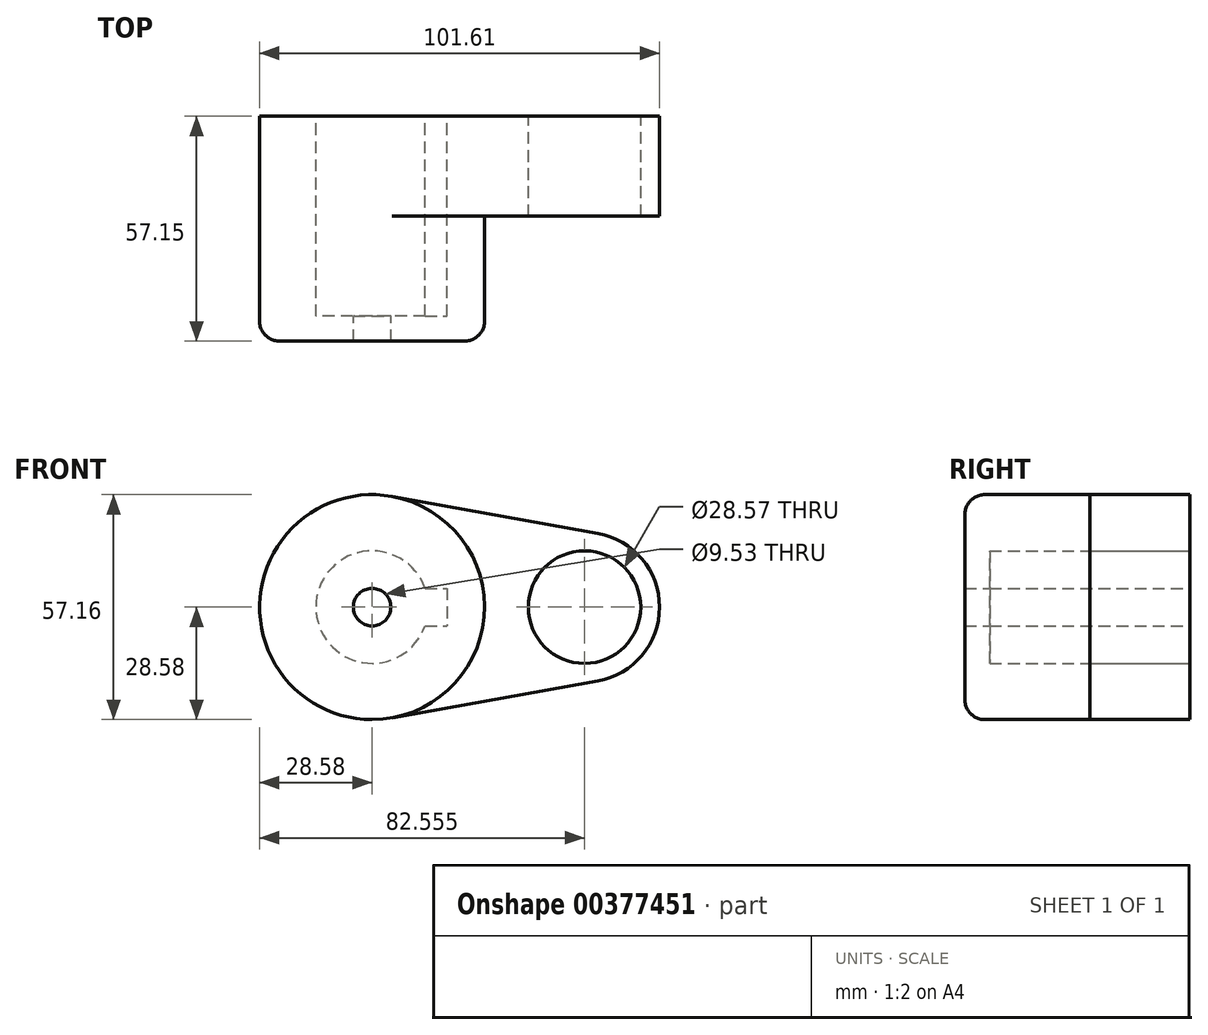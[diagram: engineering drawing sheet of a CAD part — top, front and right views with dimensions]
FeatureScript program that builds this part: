
annotation { "Feature Type Name" : "Feature", "Feature Type Description" : "" }
export const myFeature = defineFeature(function(context is Context, id is Id, definition is map)
    precondition{}
    {
        {
            var Q0;
            Q0=qCreatedBy(makeId("Front.planeOp"),FACE);
            var sketch = newSketch(context, id + "F0", { "sketchPlane" : qUnion([Q0])});
            skCircle(sketch, "E0", {"center": v(0, 0) * mm, "radius": 28.58 * mm});
            skCircle(sketch, "E1", {"center": v(53.97, 0) * mm, "radius": 19.05 * mm});
            skLineSegment(sketch, "E2", {"start": v(5.04, 28.13) * mm, "end": v(57.34, 18.75) * mm});
            skLineSegment(sketch, "E3", {"start": v(5.04, -28.13) * mm, "end": v(57.34, -18.75) * mm});
            skCircle(sketch, "E4", {"center": v(0, 0) * mm, "radius": 14.29 * mm});
            skCircle(sketch, "E5", {"center": v(53.97, 0) * mm, "radius": 14.29 * mm});
            skLineSegment(sketch, "E6.bottom", {"start": v(-19.05, 4.76) * mm, "end": v(19.05, 4.76) * mm});
            skLineSegment(sketch, "E6.top", {"start": v(-19.05, -4.76) * mm, "end": v(19.05, -4.76) * mm});
            skLineSegment(sketch, "E6.left", {"start": v(-19.05, 4.76) * mm, "end": v(-19.05, -4.76) * mm});
            skLineSegment(sketch, "E6.right", {"start": v(19.05, 4.76) * mm, "end": v(19.05, -4.76) * mm});
            skSolve(sketch);
        }
        {
            var Q0;
            {var subQ7=sQuery(id+"F0.wireOp",EDGE,"E6.left");Q0=makeQuery(id+"F0.imprint","IMPRINT",FACE,{"disambiguationData":[TD([[makeQuery(id+"F0.imprint","IMPRINT",EDGE,{"derivedFrom":subQ7}),-1.0]])]});}
            var Q1;
            {var subQ0=sQuery(id+"F0.wireOp",EDGE,"E2");Q1=makeQuery(id+"F0.imprint","IMPRINT",FACE,{"disambiguationData":[TD([[makeQuery(id+"F0.imprint","IMPRINT",EDGE,{"derivedFrom":subQ0}),-1.0]])]});}
            var Q2;
            Q2=makeQuery(id+"F0.imprint","IMPRINT",FACE,{"disambiguationData":[TD([[makeQuery(id+"F0.imprint","IMPRINT",EDGE,{"derivedFrom":sQuery(id+"F0.wireOp",EDGE,"E5")}),-1.0]])]});
            extrude(context, id + "F1", {"entities" : qUnion([Q0, Q1, Q2]), "depth" : 25.4 * mm});
        }
        {
            var Q0;
            {var subQ5=sQuery(id+"F0.wireOp",EDGE,"E6.left");Q0=makeQuery(id+"F0.imprint","IMPRINT",FACE,{"disambiguationData":[TD([[makeQuery(id+"F0.imprint","IMPRINT",EDGE,{"derivedFrom":subQ5}),1.0]])]});}
            var Q1;
            {var subQ7=sQuery(id+"F0.wireOp",EDGE,"E6.left");Q1=makeQuery(id+"F0.imprint","IMPRINT",FACE,{"disambiguationData":[TD([[makeQuery(id+"F0.imprint","IMPRINT",EDGE,{"derivedFrom":subQ7}),-1.0]])]});}
            extrude(context, id + "F2", {"entities" : qUnion([Q0, Q1]), "operationType" : NewBodyOperationType.ADD, "depth" : 50.8 * mm});
        }
        {
            var Q0;
            Q0=makeQuery(id+"F2.opExtrude","CAP_FACE",FACE,{"disambiguationData":[OSD([sQuery(id+"F0.wireOp",EDGE,"E0"),sQuery(id+"F0.wireOp",EDGE,"E4"),sQuery(id+"F0.wireOp",EDGE,"E6.bottom"),sQuery(id+"F0.wireOp",EDGE,"E6.top"),sQuery(id+"F0.wireOp",EDGE,"E6.right")])],"isStart":false});
            var sketch = newSketch(context, id + "F3", { "sketchPlane" : qUnion([Q0])});
            skCircle(sketch, "E7", {"center": v(0, 0) * mm, "radius": 28.58 * mm});
            skCircle(sketch, "E8", {"center": v(0, 0) * mm, "radius": 4.76 * mm});
            skSolve(sketch);
        }
        {
            var Q0;
            Q0 = qSketchRegion(id + "F3", true);
            extrude(context, id + "F4", {"entities" : qUnion([Q0]), "operationType" : NewBodyOperationType.ADD, "depth" : 6.35 * mm});
        }
        {
            var Q0;
            Q0=makeQuery(id+"F4.opExtrude","CAP_EDGE",EDGE,{"disambiguationData":[OSD([sQuery(id+"F3.wireOp",EDGE,"E7")])],"isStart":false});
            fillet(context, id + "F5", {"entities" : qUnion([Q0]), "radius" : 5.08 * mm, "tangentPropagation" : true, "allowEdgeOverflow" : false});
        }
    });
